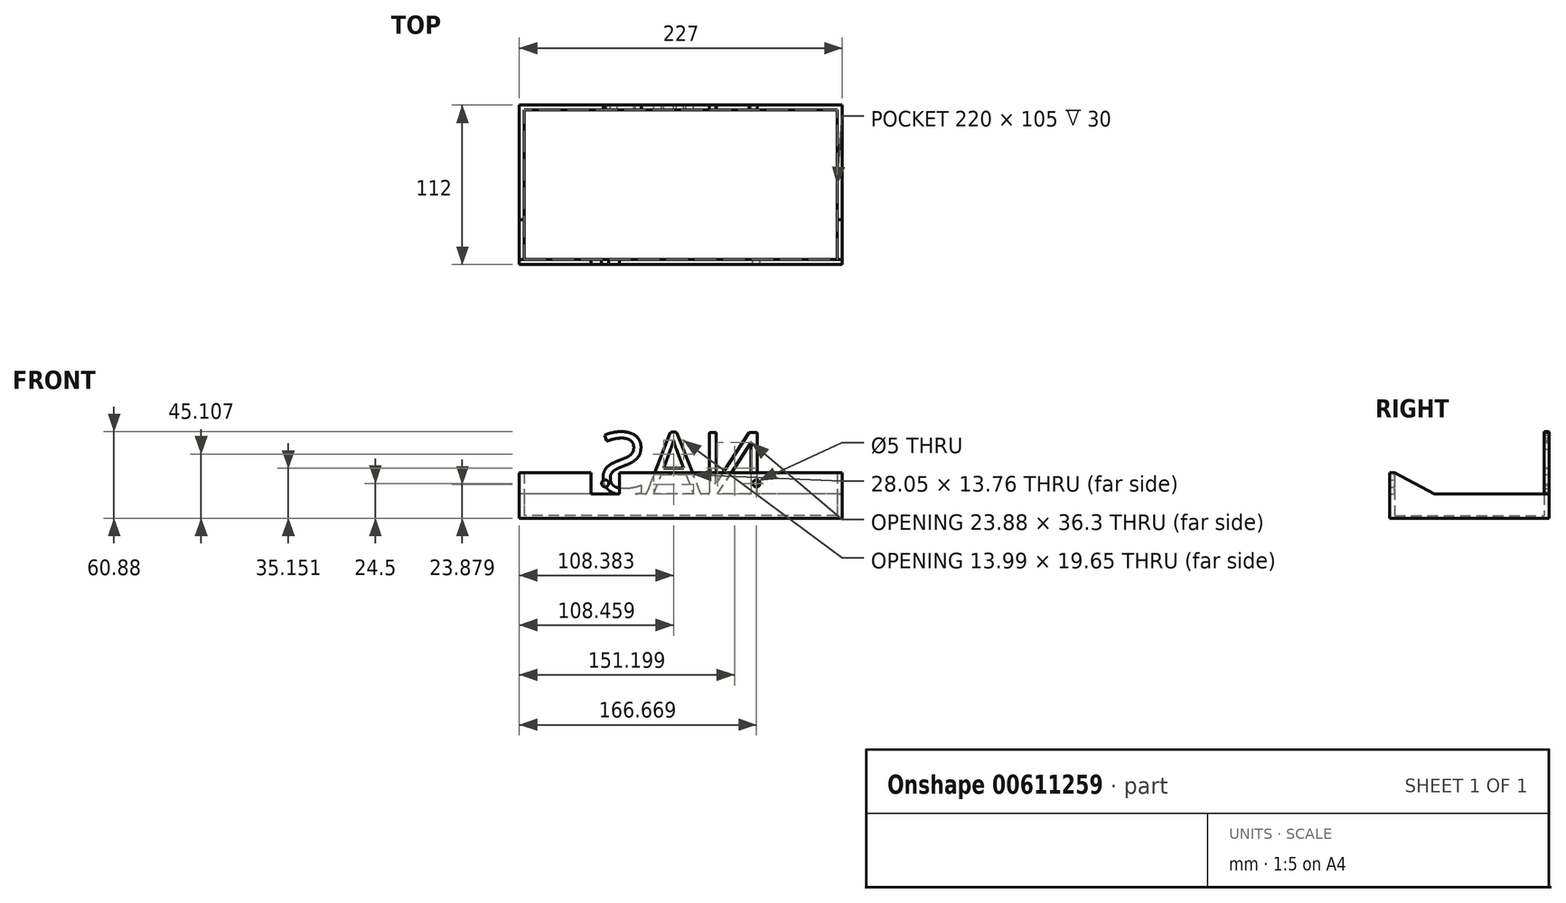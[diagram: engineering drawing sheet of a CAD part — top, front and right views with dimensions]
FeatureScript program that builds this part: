
annotation { "Feature Type Name" : "Feature", "Feature Type Description" : "" }
export const myFeature = defineFeature(function(context is Context, id is Id, definition is map)
    precondition{}
    {
        {
            var Q0;
            Q0=qCreatedBy(makeId("Top.planeOp"),FACE);
            var sketch = newSketch(context, id + "F0", { "sketchPlane" : qUnion([Q0])});
            skLineSegment(sketch, "E0.bottom", {"start": v(110, -52.5) * mm, "end": v(-110, -52.5) * mm});
            skLineSegment(sketch, "E0.top", {"start": v(110, 52.5) * mm, "end": v(-110, 52.5) * mm});
            skLineSegment(sketch, "E0.left", {"start": v(110, -52.5) * mm, "end": v(110, 52.5) * mm});
            skLineSegment(sketch, "E0.right", {"start": v(-110, -52.5) * mm, "end": v(-110, 52.5) * mm});
            skPoint(sketch, "E0.middle", {"position": v(0, 0) * mm});
            skLineSegment(sketch, "E1.0", {"start": v(-113.5, -56) * mm, "end": v(-113.5, 56) * mm});
            skLineSegment(sketch, "E1.1", {"start": v(113.5, -56) * mm, "end": v(-113.5, -56) * mm});
            skLineSegment(sketch, "E1.2", {"start": v(113.5, -56) * mm, "end": v(113.5, 56) * mm});
            skLineSegment(sketch, "E1.3", {"start": v(113.5, 56) * mm, "end": v(-113.5, 56) * mm});
            skSolve(sketch);
        }
        {
            var Q0;
            Q0=makeQuery(id+"F0.imprint","IMPRINT",FACE,{"disambiguationData":[TD([[makeQuery(id+"F0.imprint","IMPRINT",EDGE,{"derivedFrom":sQuery(id+"F0.wireOp",EDGE,"E0.bottom")}),1.0]])]});
            extrude(context, id + "F1", {"entities" : qUnion([Q0]), "depth" : 15 * mm, "offsetDistance" : 25 * mm});
        }
        {
            var Q0;
            Q0=makeQuery(id+"F1.opExtrude","CAP_FACE",FACE,{"disambiguationData":[OSD([sQuery(id+"F0.wireOp",EDGE,"E0.bottom"),sQuery(id+"F0.wireOp",EDGE,"E0.top"),sQuery(id+"F0.wireOp",EDGE,"E0.left"),sQuery(id+"F0.wireOp",EDGE,"E0.right"),sQuery(id+"F0.wireOp",EDGE,"E1.0"),sQuery(id+"F0.wireOp",EDGE,"E1.1"),sQuery(id+"F0.wireOp",EDGE,"E1.2"),sQuery(id+"F0.wireOp",EDGE,"E1.3")])],"isStart":true});
            var sketch = newSketch(context, id + "F2", { "sketchPlane" : qUnion([Q0])});
            skLineSegment(sketch, "E2.0", {"start": v(-113.5, 56) * mm, "end": v(-113.5, -56) * mm});
            skLineSegment(sketch, "E3.0", {"start": v(113.5, 56) * mm, "end": v(-113.5, 56) * mm});
            skLineSegment(sketch, "E4.0", {"start": v(113.5, 56) * mm, "end": v(113.5, -56) * mm});
            skLineSegment(sketch, "E5.0", {"start": v(113.5, -56) * mm, "end": v(-113.5, -56) * mm});
            skSolve(sketch);
        }
        {
            var Q0;
            Q0=makeQuery(id+"F2.imprint","IMPRINT",FACE,{"disambiguationData":[TD([[makeQuery(id+"F2.imprint","IMPRINT",EDGE,{"derivedFrom":makeQuery(id+"F1.opExtrude","CAP_EDGE",EDGE,{"disambiguationData":[OSD([sQuery(id+"F0.wireOp",EDGE,"E0.bottom")])],"isStart":true})}),1.0]])]});
            var Q1;
            Q1=makeQuery(id+"F2.imprint","IMPRINT",FACE,{"disambiguationData":[TD([[makeQuery(id+"F2.imprint","IMPRINT",EDGE,{"derivedFrom":sQuery(id+"F2.wireOp",EDGE,"E2.0")}),1.0]])]});
            extrude(context, id + "F3", {"entities" : qUnion([Q0, Q1]), "operationType" : NewBodyOperationType.ADD, "depth" : 2 * mm, "offsetDistance" : 25 * mm});
        }
        {
            var Q0;
            Q0=makeQuery(id+"F1.opExtrude","SWEPT_FACE",FACE,{"disambiguationData":[OSD([sQuery(id+"F0.wireOp",EDGE,"E0.bottom")])]});
            var sketch = newSketch(context, id + "F4", { "sketchPlane" : qUnion([Q0])});
            skLineSegment(sketch, "E6.bottom", {"start": v(-63.17, 15) * mm, "end": v(-43.17, 15) * mm});
            skLineSegment(sketch, "E6.top", {"start": v(-63.17, 30) * mm, "end": v(-43.17, 30) * mm});
            skLineSegment(sketch, "E6.left", {"start": v(-63.17, 15) * mm, "end": v(-63.17, 30) * mm});
            skLineSegment(sketch, "E6.right", {"start": v(-43.17, 15) * mm, "end": v(-43.17, 30) * mm});
            skCircle(sketch, "E7", {"center": v(-53.17, 22.5) * mm, "radius": 2.5 * mm});
            skPoint(sketch, "E7.centerSnap0", {"position": v(-63.17, 22.5) * mm});
            skPoint(sketch, "E7.centerSnap1", {"position": v(-53.17, 30) * mm});
            skCircle(sketch, "E8.MirrorC", {"center": v(53.17, 22.5) * mm, "radius": 2.5 * mm});
            skLineSegment(sketch, "E9.MirrorCS", {"start": v(43.17, 15) * mm, "end": v(43.17, 30) * mm});
            skLineSegment(sketch, "E10.MirrorCS", {"start": v(63.17, 15) * mm, "end": v(63.17, 30) * mm});
            skLineSegment(sketch, "E11.MirrorCS", {"start": v(63.17, 30) * mm, "end": v(43.17, 30) * mm});
            skLineSegment(sketch, "E12.MirrorCS", {"start": v(63.17, 15) * mm, "end": v(43.17, 15) * mm});
            skPoint(sketch, "E13.MirrorP", {"position": v(53.17, 30) * mm});
            skPoint(sketch, "E14.MirrorP", {"position": v(63.17, 22.5) * mm});
            skLineSegment(sketch, "E15", {"start": v(-53.17, 30) * mm, "end": v(53.17, 30) * mm, "construction": true});
            skLineSegment(sketch, "E16.0", {"start": v(-113.5, 15) * mm, "end": v(-113.5, -2) * mm});
            skLineSegment(sketch, "E17.0", {"start": v(113.5, 15) * mm, "end": v(113.5, -2) * mm});
            skLineSegment(sketch, "E18", {"start": v(-113.5, 15) * mm, "end": v(-113.5, 30) * mm});
            skLineSegment(sketch, "E19", {"start": v(-113.5, 30) * mm, "end": v(-63.17, 30) * mm});
            skLineSegment(sketch, "E20", {"start": v(-43.17, 30) * mm, "end": v(43.17, 30) * mm});
            skLineSegment(sketch, "E21", {"start": v(63.17, 30) * mm, "end": v(113.5, 30) * mm});
            skLineSegment(sketch, "E22", {"start": v(113.5, 30) * mm, "end": v(113.5, 15) * mm});
            skLineSegment(sketch, "E23", {"start": v(-113.5, 15) * mm, "end": v(-63.17, 15) * mm});
            skLineSegment(sketch, "E24", {"start": v(-43.17, 15) * mm, "end": v(43.17, 15) * mm});
            skLineSegment(sketch, "E25", {"start": v(113.5, 15) * mm, "end": v(63.17, 15) * mm});
            skSolve(sketch);
        }
        {
            var Q0;
            Q0=makeQuery(id+"F4.imprint","IMPRINT",FACE,{"disambiguationData":[TD([[makeQuery(id+"F4.imprint","IMPRINT",EDGE,{"derivedFrom":sQuery(id+"F4.wireOp",EDGE,"E6.bottom")}),1.0]])]});
            var Q1;
            Q1=makeQuery(id+"F4.imprint","IMPRINT",FACE,{"disambiguationData":[TD([[makeQuery(id+"F4.imprint","IMPRINT",EDGE,{"derivedFrom":sQuery(id+"F4.wireOp",EDGE,"E8.MirrorC")}),1.0]])]});
            var Q2;
            {var subQ2=sQuery(id+"F4.wireOp",EDGE,"E6.left");Q2=makeQuery(id+"F4.imprint","IMPRINT",FACE,{"disambiguationData":[TD([[makeQuery(id+"F4.imprint","IMPRINT",EDGE,{"derivedFrom":subQ2}),1.0]])]});}
            var Q3;
            Q3=makeQuery(id+"F4.imprint","IMPRINT",FACE,{"disambiguationData":[TD([[makeQuery(id+"F4.imprint","IMPRINT",EDGE,{"derivedFrom":sQuery(id+"F4.wireOp",EDGE,"E6.right")}),-1.0]])]});
            var Q4;
            {var subQ3=sQuery(id+"F4.wireOp",EDGE,"E10.MirrorCS");Q4=makeQuery(id+"F4.imprint","IMPRINT",FACE,{"disambiguationData":[TD([[makeQuery(id+"F4.imprint","IMPRINT",EDGE,{"derivedFrom":subQ3}),-1.0]])]});}
            var Q5;
            Q5=makeQuery(id+"F3.boolean.opBoolean","MERGE",FACE,{"derivedFrom":[makeQuery(id+"F1.opExtrude","SWEPT_FACE",FACE,{"disambiguationData":[OSD([sQuery(id+"F0.wireOp",EDGE,"E1.1")])]}),makeQuery(id+"F3.opExtrude","SWEPT_FACE",FACE,{"disambiguationData":[OSD([sQuery(id+"F2.wireOp",EDGE,"E3.0")])]})]});
            extrude(context, id + "F5", {"entities" : qUnion([Q0, Q1, Q2, Q3, Q4]), "operationType" : NewBodyOperationType.ADD, "endBound" : BoundingType.UP_TO_SURFACE, "oppositeDirection" : true, "depth" : 2.8 * mm, "endBoundEntityFace" : qUnion([Q5]), "offsetDistance" : 25 * mm});
        }
        {
            var Q0;
            Q0=makeQuery(id+"F3.boolean.opBoolean","MERGE",FACE,{"derivedFrom":[makeQuery(id+"F1.opExtrude","SWEPT_FACE",FACE,{"disambiguationData":[OSD([sQuery(id+"F0.wireOp",EDGE,"E1.3")])]}),makeQuery(id+"F3.opExtrude","SWEPT_FACE",FACE,{"disambiguationData":[OSD([sQuery(id+"F2.wireOp",EDGE,"E5.0")])]})]});
            var sketch = newSketch(context, id + "F6", { "sketchPlane" : qUnion([Q0])});
            skLineSegment(sketch, "E26.0", {"start": v(-113.5, 15) * mm, "end": v(113.5, 15) * mm});
            skLineSegment(sketch, "E27.bottom", {"start": v(-79.42, 15) * mm, "end": v(80.58, 15) * mm});
            skLineSegment(sketch, "E27.top", {"start": v(-79.42, 60) * mm, "end": v(80.58, 60) * mm});
            skLineSegment(sketch, "E27.left", {"start": v(-79.42, 15) * mm, "end": v(-79.42, 60) * mm});
            skLineSegment(sketch, "E27.right", {"start": v(80.58, 15) * mm, "end": v(80.58, 60) * mm});
            skText(sketch, "E28", { "text": "NAS", "fontName": "OpenSans-Regular.ttf"});
            skLineSegment(sketch, "E29.bottom", {"start": v(-55.9, 15) * mm, "end": v(56.15, 15) * mm});
            skLineSegment(sketch, "E30.0", {"start": v(-56.9, 14) * mm, "end": v(-56.9, 59.63) * mm});
            skLineSegment(sketch, "E30.1", {"start": v(-56.9, 14) * mm, "end": v(57.15, 14) * mm});
            skLineSegment(sketch, "E30.2", {"start": v(57.15, 14) * mm, "end": v(57.15, 59.63) * mm});
            skLineSegment(sketch, "E30.3", {"start": v(-56.9, 59.63) * mm, "end": v(57.15, 59.63) * mm});
            const initialGuessF6  = {"E28": [-0.05976, 0.015, 1, 0, 0.04363]};
            skSetInitialGuess(sketch, initialGuessF6);
            skSolve(sketch);
        }
        {
            var Q0;
            Q0=makeQuery(id+"F6.imprint","IMPRINT",FACE,{"disambiguationData":[TD([[makeQuery(id+"F6.imprint","IMPRINT",EDGE,{"derivedFrom":sQuery(id+"F6.wireOp",EDGE,"E28.sketch_text.stroke-0")}),1.0]])]});
            var Q1;
            Q1=makeQuery(id+"F6.imprint","IMPRINT",FACE,{"disambiguationData":[TD([[makeQuery(id+"F6.imprint","IMPRINT",EDGE,{"derivedFrom":sQuery(id+"F6.wireOp",EDGE,"E28.sketch_text.stroke-15")}),-1.0]])]});
            var Q2;
            {var subQ6=sQuery(id+"F6.wireOp",EDGE,"E28.sketch_text.stroke-28");Q2=makeQuery(id+"F6.imprint","IMPRINT",FACE,{"disambiguationData":[TD([[makeQuery(id+"F6.imprint","IMPRINT",EDGE,{"derivedFrom":subQ6}),-1.0]])]});}
            var Q3;
            {var subQ1=sQuery(id+"F6.wireOp",EDGE,"E28.sketch_text.stroke-1");Q3=makeQuery(id+"F6.imprint","IMPRINT",FACE,{"disambiguationData":[TD([[makeQuery(id+"F6.imprint","IMPRINT",EDGE,{"derivedFrom":subQ1}),-1.0]])]});}
            var Q4;
            Q4=makeQuery(id+"F1.opExtrude","SWEPT_FACE",FACE,{"disambiguationData":[OSD([sQuery(id+"F0.wireOp",EDGE,"E0.top")])]});
            extrude(context, id + "F7", {"entities" : qUnion([Q0, Q1, Q2, Q3]), "operationType" : NewBodyOperationType.ADD, "endBound" : BoundingType.UP_TO_SURFACE, "oppositeDirection" : true, "depth" : 3.3 * mm, "endBoundEntityFace" : qUnion([Q4]), "offsetDistance" : 25 * mm});
        }
        {
            var Q0;
            Q0=makeQuery(id+"F7.opExtrude","SWEPT_EDGE",EDGE,{"disambiguationData":[OSD([sQuery(id+"F6.wireOp",EDGE,"E28.sketch_text.stroke-6"),sQuery(id+"F6.wireOp",EDGE,"E29.bottom")])]});
            var Q1;
            Q1=makeQuery(id+"F7.opExtrude","SWEPT_EDGE",EDGE,{"disambiguationData":[OSD([sQuery(id+"F6.wireOp",EDGE,"E28.sketch_text.stroke-4"),sQuery(id+"F6.wireOp",EDGE,"E29.bottom")])]});
            var Q2;
            Q2=makeQuery(id+"F7.opExtrude","SWEPT_EDGE",EDGE,{"disambiguationData":[OSD([sQuery(id+"F6.wireOp",EDGE,"E28.sketch_text.stroke-14"),sQuery(id+"F6.wireOp",EDGE,"E29.bottom")])]});
            var Q3;
            Q3=makeQuery(id+"F7.opExtrude","SWEPT_EDGE",EDGE,{"disambiguationData":[OSD([sQuery(id+"F6.wireOp",EDGE,"E28.sketch_text.stroke-19"),sQuery(id+"F6.wireOp",EDGE,"E29.bottom")])]});
            var Q4;
            Q4=makeQuery(id+"F7.opExtrude","SWEPT_EDGE",EDGE,{"disambiguationData":[OSD([sQuery(id+"F6.wireOp",EDGE,"E28.sketch_text.stroke-21"),sQuery(id+"F6.wireOp",EDGE,"E29.bottom")])]});
            fillet(context, id + "F8", {"entities" : qUnion([Q0, Q1, Q2, Q3, Q4]), "radius" : 1 * mm, "tangentPropagation" : true, "allowEdgeOverflow" : false});
        }
        {
            var Q0;
            Q0=makeQuery(id+"F5.boolean.opBoolean","MERGE",FACE,{"derivedFrom":[makeQuery(id+"F3.boolean.opBoolean","MERGE",FACE,{"derivedFrom":[makeQuery(id+"F1.opExtrude","SWEPT_FACE",FACE,{"disambiguationData":[OSD([sQuery(id+"F0.wireOp",EDGE,"E1.2")])]}),makeQuery(id+"F3.opExtrude","SWEPT_FACE",FACE,{"disambiguationData":[OSD([sQuery(id+"F2.wireOp",EDGE,"E4.0")])]})]}),makeQuery(id+"F5.opExtrude","SWEPT_FACE",FACE,{"disambiguationData":[OSD([sQuery(id+"F4.wireOp",EDGE,"E18")])]})]});
            var sketch = newSketch(context, id + "F9", { "sketchPlane" : qUnion([Q0])});
            skLineSegment(sketch, "E31", {"start": v(-52.5, 30) * mm, "end": v(-24.52, 15) * mm});
            skLineSegment(sketch, "E32", {"start": v(-24.52, 15) * mm, "end": v(-52.5, 15) * mm});
            skLineSegment(sketch, "E33", {"start": v(-52.5, 15) * mm, "end": v(-52.5, 30) * mm});
            skSolve(sketch);
        }
        {
            var Q0;
            Q0=makeQuery(id+"F5.boolean.opBoolean","MERGE",FACE,{"derivedFrom":[makeQuery(id+"F3.boolean.opBoolean","MERGE",FACE,{"derivedFrom":[makeQuery(id+"F1.opExtrude","SWEPT_FACE",FACE,{"disambiguationData":[OSD([sQuery(id+"F0.wireOp",EDGE,"E1.0")])]}),makeQuery(id+"F3.opExtrude","SWEPT_FACE",FACE,{"disambiguationData":[OSD([sQuery(id+"F2.wireOp",EDGE,"E2.0")])]})]}),makeQuery(id+"F5.opExtrude","SWEPT_FACE",FACE,{"disambiguationData":[OSD([sQuery(id+"F4.wireOp",EDGE,"E22")])]})]});
            var sketch = newSketch(context, id + "F10", { "sketchPlane" : qUnion([Q0])});
            skLineSegment(sketch, "E34", {"start": v(52.5, 30) * mm, "end": v(24.68, 15) * mm});
            skLineSegment(sketch, "E35", {"start": v(24.68, 15) * mm, "end": v(52.5, 15) * mm});
            skLineSegment(sketch, "E36", {"start": v(52.5, 15) * mm, "end": v(52.5, 30) * mm});
            skSolve(sketch);
        }
        {
            var Q0;
            Q0=makeQuery(id+"F9.imprint","IMPRINT",FACE,{"disambiguationData":[TD([[makeQuery(id+"F9.imprint","IMPRINT",EDGE,{"derivedFrom":sQuery(id+"F9.wireOp",EDGE,"E31")}),-1.0]])]});
            extrude(context, id + "F11", {"entities" : qUnion([Q0]), "operationType" : NewBodyOperationType.ADD, "oppositeDirection" : true, "depth" : 3.5 * mm, "offsetDistance" : 25 * mm});
        }
        {
            var Q0;
            Q0=makeQuery(id+"F10.imprint","IMPRINT",FACE,{"disambiguationData":[TD([[makeQuery(id+"F10.imprint","IMPRINT",EDGE,{"derivedFrom":sQuery(id+"F10.wireOp",EDGE,"E34")}),1.0]])]});
            extrude(context, id + "F12", {"entities" : qUnion([Q0]), "operationType" : NewBodyOperationType.ADD, "oppositeDirection" : true, "depth" : 3.5 * mm, "offsetDistance" : 25 * mm});
        }
    });
